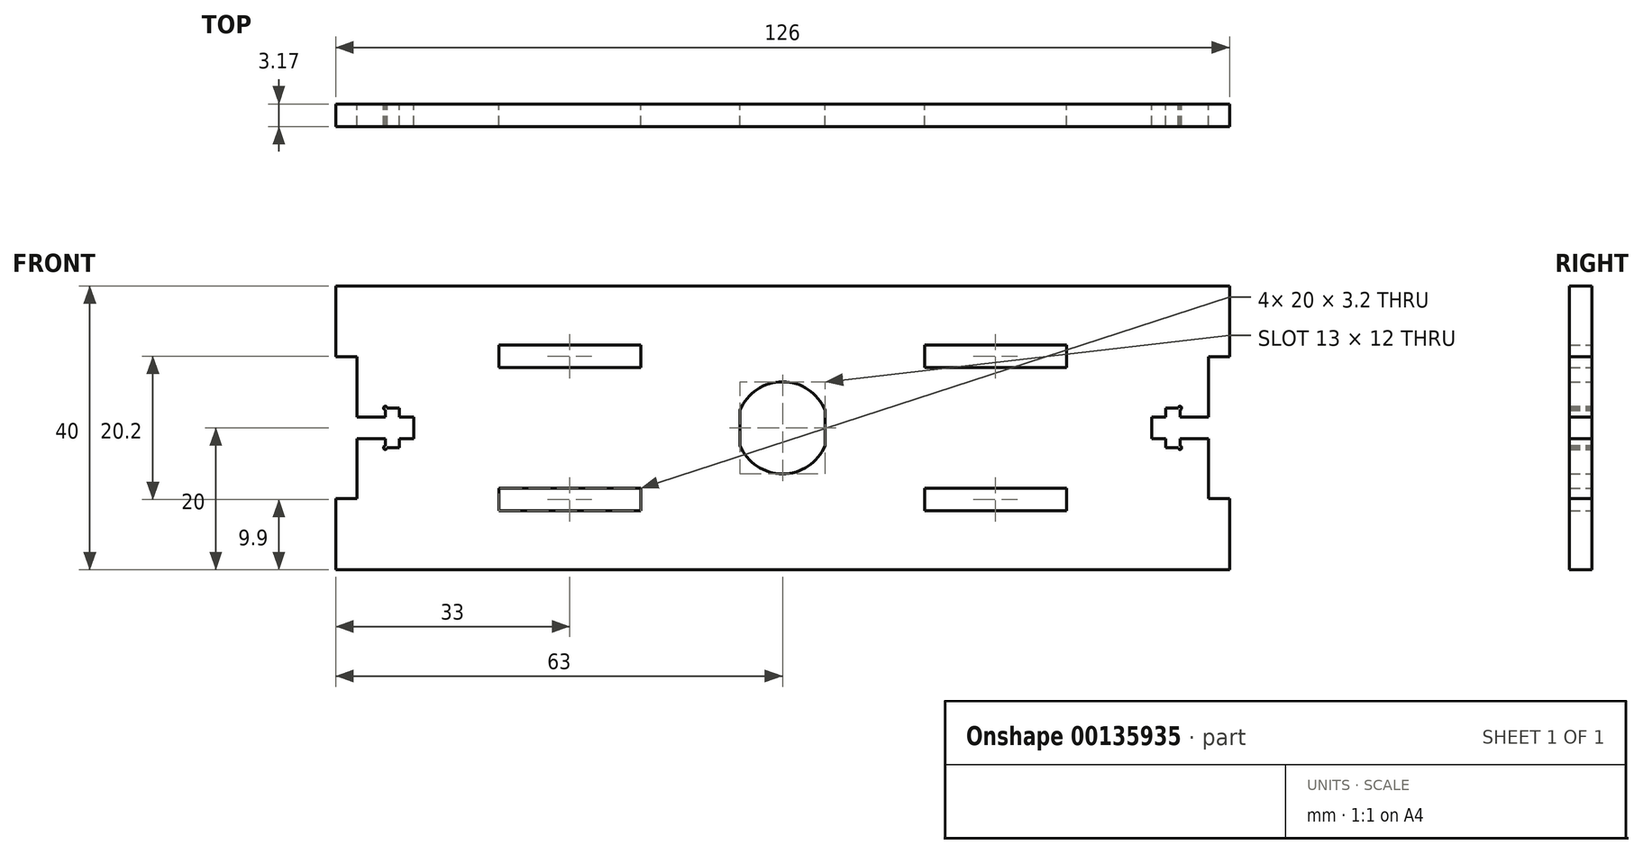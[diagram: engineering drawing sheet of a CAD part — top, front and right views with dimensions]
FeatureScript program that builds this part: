
annotation { "Feature Type Name" : "Feature", "Feature Type Description" : "" }
export const myFeature = defineFeature(function(context is Context, id is Id, definition is map)
    precondition{}
    {
        {
            var Q0;
            Q0=qCreatedBy(makeId("Front.planeOp"),FACE);
            var sketch = newSketch(context, id + "F0", { "sketchPlane" : qUnion([Q0])});
            skLineSegment(sketch, "E0", {"start": v(0, 20) * mm, "end": v(63, 20) * mm});
            skLineSegment(sketch, "E1", {"start": v(63, 20) * mm, "end": v(63, 10) * mm});
            skLineSegment(sketch, "E2", {"start": v(63, 10) * mm, "end": v(60, 10) * mm});
            skLineSegment(sketch, "E3", {"start": v(60, 10) * mm, "end": v(60, 1.55) * mm});
            skLineSegment(sketch, "E4", {"start": v(60, 1.55) * mm, "end": v(56, 1.55) * mm});
            skLineSegment(sketch, "E5", {"start": v(56, 1.55) * mm, "end": v(56, 2.8) * mm});
            skLineSegment(sketch, "E6", {"start": v(56, 2.8) * mm, "end": v(54, 2.8) * mm});
            skLineSegment(sketch, "E7", {"start": v(54, 2.8) * mm, "end": v(54, 1.55) * mm});
            skLineSegment(sketch, "E8", {"start": v(54, 1.55) * mm, "end": v(52, 1.55) * mm});
            skLineSegment(sketch, "E9", {"start": v(52, 1.55) * mm, "end": v(52, 0) * mm});
            skCircle(sketch, "E10", {"center": v(56, 2.8) * mm, "radius": 0.25 * mm});
            skCircle(sketch, "E11.MirrorC", {"center": v(56, -2.8) * mm, "radius": 0.25 * mm});
            skLineSegment(sketch, "E12.MirrorCS", {"start": v(54, -2.8) * mm, "end": v(54, -1.55) * mm});
            skLineSegment(sketch, "E13.MirrorCS", {"start": v(56, -2.8) * mm, "end": v(54, -2.8) * mm});
            skLineSegment(sketch, "E14.MirrorCS", {"start": v(56, -1.55) * mm, "end": v(56, -2.8) * mm});
            skLineSegment(sketch, "E15.MirrorCS", {"start": v(52, -1.55) * mm, "end": v(52, 0) * mm});
            skLineSegment(sketch, "E16.MirrorCS", {"start": v(54, -1.55) * mm, "end": v(52, -1.55) * mm});
            skLineSegment(sketch, "E17.MirrorCS", {"start": v(0, -20) * mm, "end": v(63, -20) * mm});
            skLineSegment(sketch, "E18.MirrorCS", {"start": v(63, -20) * mm, "end": v(63, -10) * mm});
            skLineSegment(sketch, "E19.MirrorCS", {"start": v(63, -10) * mm, "end": v(60, -10) * mm});
            skLineSegment(sketch, "E20.MirrorCS", {"start": v(60, -10) * mm, "end": v(60, -1.55) * mm});
            skLineSegment(sketch, "E21.MirrorCS", {"start": v(60, -1.55) * mm, "end": v(56, -1.55) * mm});
            skCircle(sketch, "E22.MirrorC", {"center": v(-56, -2.8) * mm, "radius": 0.25 * mm});
            skCircle(sketch, "E23.MirrorC", {"center": v(-56, 2.8) * mm, "radius": 0.25 * mm});
            skLineSegment(sketch, "E24.MirrorCS", {"start": v(-56, -2.8) * mm, "end": v(-54, -2.8) * mm});
            skLineSegment(sketch, "E25.MirrorCS", {"start": v(-56, 1.55) * mm, "end": v(-56, 2.8) * mm});
            skLineSegment(sketch, "E26.MirrorCS", {"start": v(-54, -2.8) * mm, "end": v(-54, -1.55) * mm});
            skLineSegment(sketch, "E27.MirrorCS", {"start": v(-56, 2.8) * mm, "end": v(-54, 2.8) * mm});
            skLineSegment(sketch, "E28.MirrorCS", {"start": v(-54, 2.8) * mm, "end": v(-54, 1.55) * mm});
            skLineSegment(sketch, "E29.MirrorCS", {"start": v(-52, 1.55) * mm, "end": v(-52, 0) * mm});
            skLineSegment(sketch, "E30.MirrorCS", {"start": v(-52, -1.55) * mm, "end": v(-52, 0) * mm});
            skLineSegment(sketch, "E31.MirrorCS", {"start": v(-56, -1.55) * mm, "end": v(-56, -2.8) * mm});
            skLineSegment(sketch, "E32.MirrorCS", {"start": v(-54, -1.55) * mm, "end": v(-52, -1.55) * mm});
            skLineSegment(sketch, "E33.MirrorCS", {"start": v(-63, -20) * mm, "end": v(-63, -10) * mm});
            skLineSegment(sketch, "E34.MirrorCS", {"start": v(-60, -10) * mm, "end": v(-60, -1.55) * mm});
            skLineSegment(sketch, "E35.MirrorCS", {"start": v(-60, -1.55) * mm, "end": v(-56, -1.55) * mm});
            skLineSegment(sketch, "E36.MirrorCS", {"start": v(-63, -10) * mm, "end": v(-60, -10) * mm});
            skLineSegment(sketch, "E37.MirrorCS", {"start": v(-63, 10) * mm, "end": v(-60, 10) * mm});
            skLineSegment(sketch, "E38.MirrorCS", {"start": v(0, -20) * mm, "end": v(-63, -20) * mm});
            skLineSegment(sketch, "E39.MirrorCS", {"start": v(-60, 1.55) * mm, "end": v(-56, 1.55) * mm});
            skLineSegment(sketch, "E40.MirrorCS", {"start": v(-63, 20) * mm, "end": v(-63, 10) * mm});
            skLineSegment(sketch, "E41.MirrorCS", {"start": v(-54, 1.55) * mm, "end": v(-52, 1.55) * mm});
            skLineSegment(sketch, "E42.MirrorCS", {"start": v(-60, 10) * mm, "end": v(-60, 1.55) * mm});
            skLineSegment(sketch, "E43.MirrorCS", {"start": v(0, 20) * mm, "end": v(-63, 20) * mm});
            skLineSegment(sketch, "E44.bottom", {"start": v(20, 11.7) * mm, "end": v(40, 11.7) * mm});
            skLineSegment(sketch, "E44.top", {"start": v(20, 8.5) * mm, "end": v(40, 8.5) * mm});
            skLineSegment(sketch, "E44.left", {"start": v(20, 11.7) * mm, "end": v(20, 8.5) * mm});
            skLineSegment(sketch, "E44.right", {"start": v(40, 11.7) * mm, "end": v(40, 8.5) * mm});
            skLineSegment(sketch, "E45.MirrorCS", {"start": v(40, -11.7) * mm, "end": v(40, -8.5) * mm});
            skLineSegment(sketch, "E46.MirrorCS", {"start": v(20, -11.7) * mm, "end": v(20, -8.5) * mm});
            skLineSegment(sketch, "E47.MirrorCS", {"start": v(20, -8.5) * mm, "end": v(40, -8.5) * mm});
            skLineSegment(sketch, "E48.MirrorCS", {"start": v(20, -11.7) * mm, "end": v(40, -11.7) * mm});
            skLineSegment(sketch, "E49.MirrorCS", {"start": v(-20, -11.7) * mm, "end": v(-40, -11.7) * mm});
            skLineSegment(sketch, "E50.MirrorCS", {"start": v(-20, -8.5) * mm, "end": v(-40, -8.5) * mm});
            skLineSegment(sketch, "E51.MirrorCS", {"start": v(-20, -11.7) * mm, "end": v(-20, -8.5) * mm});
            skLineSegment(sketch, "E52.MirrorCS", {"start": v(-20, 11.7) * mm, "end": v(-20, 8.5) * mm});
            skLineSegment(sketch, "E53.MirrorCS", {"start": v(-20, 11.7) * mm, "end": v(-40, 11.7) * mm});
            skLineSegment(sketch, "E54.MirrorCS", {"start": v(-40, -11.7) * mm, "end": v(-40, -8.5) * mm});
            skLineSegment(sketch, "E55.MirrorCS", {"start": v(-40, 11.7) * mm, "end": v(-40, 8.5) * mm});
            skLineSegment(sketch, "E56.MirrorCS", {"start": v(-20, 8.5) * mm, "end": v(-40, 8.5) * mm});
            skPoint(sketch, "E57.middle", {"position": v(0, 0) * mm});
            skPoint(sketch, "E58", {"position": v(-6, 2.5) * mm});
            skPoint(sketch, "E59", {"position": v(-6, -2.5) * mm});
            skPoint(sketch, "E60", {"position": v(6, -2.5) * mm});
            skPoint(sketch, "E61", {"position": v(6, 2.5) * mm});
            skArc(sketch, "E62", {"start": v(-6, 2.5) * mm, "mid": v(0, 6.5) * mm, "end": v(6, 2.5) * mm});
            skArc(sketch, "E63", {"start": v(-6, -2.5) * mm, "mid": v(0, -6.5) * mm, "end": v(6, -2.5) * mm});
            skLineSegment(sketch, "E64", {"start": v(-6, 2.5) * mm, "end": v(-6, -2.5) * mm});
            skLineSegment(sketch, "E65", {"start": v(6, 2.5) * mm, "end": v(6, -2.5) * mm});
            skSolve(sketch);
        }
        {
            var Q0;
            Q0=makeQuery(id+"F0.imprint","IMPRINT",FACE,{"disambiguationData":[TD([[makeQuery(id+"F0.imprint","IMPRINT",EDGE,{"derivedFrom":sQuery(id+"F0.wireOp",EDGE,"E0")}),-1.0]])]});
            extrude(context, id + "F1", {"entities" : qUnion([Q0]), "depth" : 3.17 * mm});
        }
    });
